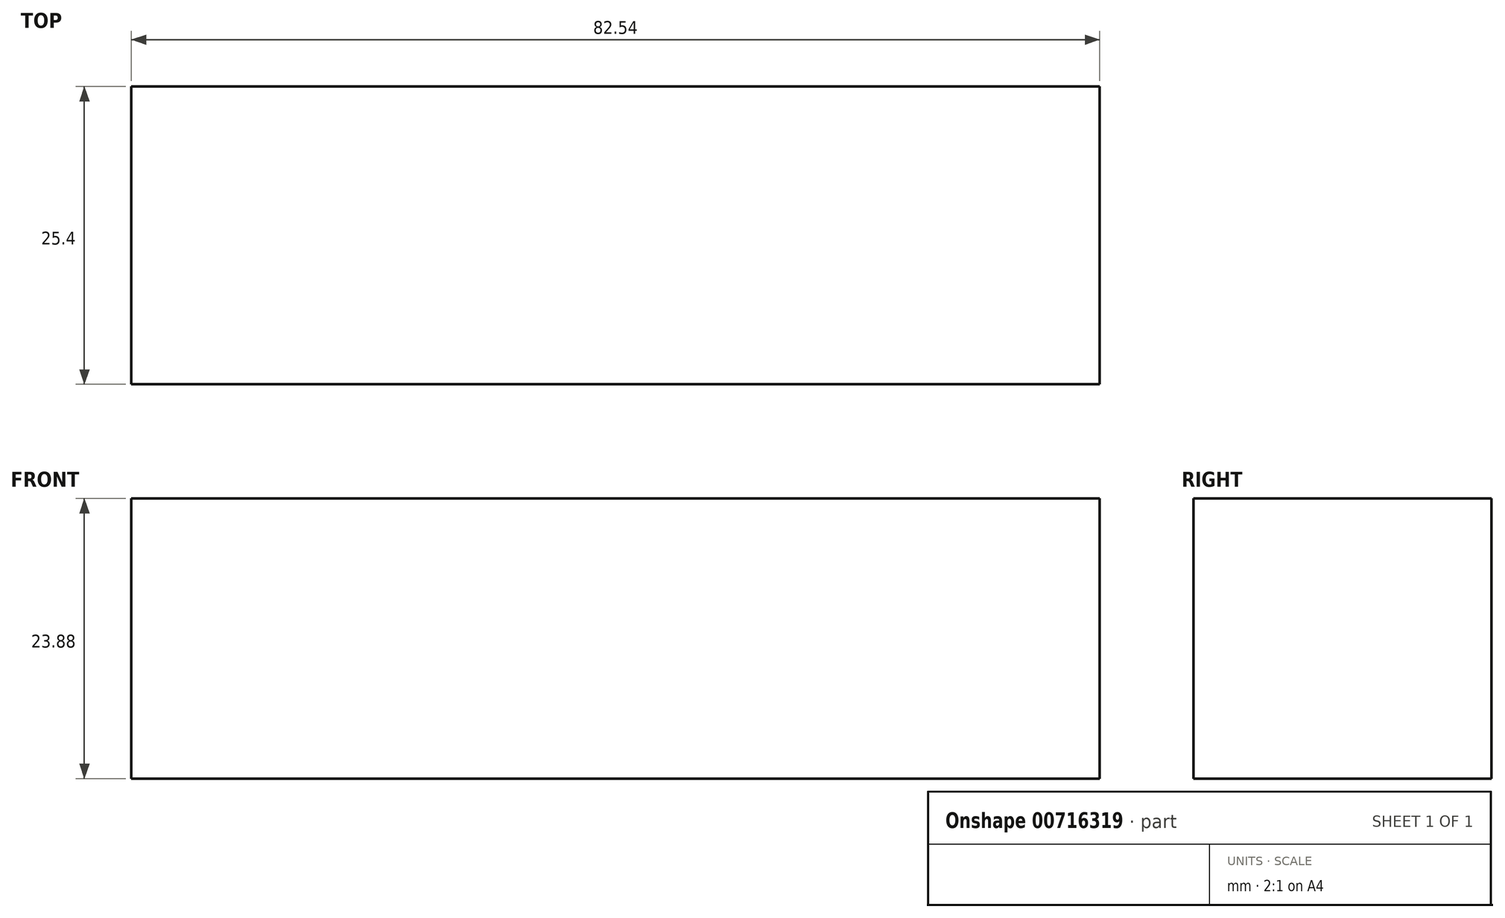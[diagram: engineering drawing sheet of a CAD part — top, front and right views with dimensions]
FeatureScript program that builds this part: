
annotation { "Feature Type Name" : "Feature", "Feature Type Description" : "" }
export const myFeature = defineFeature(function(context is Context, id is Id, definition is map)
    precondition{}
    {
        {
            var Q0;
            Q0=qCreatedBy(makeId("Front.planeOp"),FACE);
            var sketch = newSketch(context, id + "F0", { "sketchPlane" : qUnion([Q0])});
            skLineSegment(sketch, "E0.bottom", {"start": v(-41.27, 11.94) * mm, "end": v(41.27, 11.94) * mm});
            skLineSegment(sketch, "E0.top", {"start": v(-41.27, -11.94) * mm, "end": v(41.27, -11.94) * mm});
            skLineSegment(sketch, "E0.left", {"start": v(-41.28, 11.94) * mm, "end": v(-41.28, -11.94) * mm});
            skLineSegment(sketch, "E0.right", {"start": v(41.28, 11.94) * mm, "end": v(41.28, -11.94) * mm});
            skPoint(sketch, "E0.middle", {"position": v(0, 0) * mm});
            skLineSegment(sketch, "E1", {"start": v(41.28, 11.94) * mm, "end": v(41.28, 32.5) * mm});
            skArc(sketch, "E2", {"start": v(41.27, 32.5) * mm, "mid": v(47.74, 47.55) * mm, "end": v(63.1, 53.22) * mm});
            skLineSegment(sketch, "E3.bottom", {"start": v(98.61, 79.01) * mm, "end": v(139.25, 79.01) * mm});
            skLineSegment(sketch, "E3.top", {"start": v(98.61, 38.63) * mm, "end": v(139.25, 38.63) * mm});
            skLineSegment(sketch, "E3.left", {"start": v(98.61, 79.01) * mm, "end": v(98.61, 38.63) * mm});
            skLineSegment(sketch, "E3.right", {"start": v(139.25, 79.01) * mm, "end": v(139.25, 38.63) * mm});
            skLineSegment(sketch, "E4", {"start": v(63.1, 53.22) * mm, "end": v(125.6, 53.22) * mm});
            skLineSegment(sketch, "E5.0", {"start": v(63.52, 72.5) * mm, "end": v(125.6, 72.5) * mm});
            skArc(sketch, "E5.1", {"start": v(22, 32.5) * mm, "mid": v(34.25, 61.33) * mm, "end": v(63.52, 72.5) * mm});
            skLineSegment(sketch, "E5.2", {"start": v(22, 11.94) * mm, "end": v(22, 32.5) * mm});
            skLineSegment(sketch, "E6", {"start": v(-41.27, 11.94) * mm, "end": v(63.52, 72.5) * mm});
            skSolve(sketch);
        }
        {
            var Q0;
            Q0=makeQuery(id+"F0.imprint","IMPRINT",FACE,{"disambiguationData":[TD([[makeQuery(id+"F0.imprint","IMPRINT",EDGE,{"derivedFrom":sQuery(id+"F0.wireOp",EDGE,"E0.top")}),1.0]])]});
            extrude(context, id + "F1", {"entities" : qUnion([Q0]), "oppositeDirection" : true, "depth" : 25.4 * mm, "offsetDistance" : 25.4 * mm});
        }
    });
